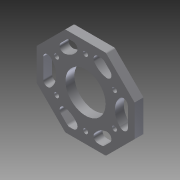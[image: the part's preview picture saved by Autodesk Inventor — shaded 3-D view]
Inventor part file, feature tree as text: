
AUTODESK INVENTOR PART (.ipt)
format: ipt  version: 2012 (Build 160160000, 160)  size: 216,576 bytes
history: native  units: in
note: dims shown in document units (in); Inventor stores cm internally (conversion verified against a paired STEP export)
features: fillet x2, sketch x1, extrude x1
ambient origin geometry x8: Origin, YZ Plane, XZ Plane, XY Plane, X Axis, Y Axis, Z Axis, Center Point
bodies: Solid1 (feature_tree)
feature tree (4):
  sketch  "Sketch1"  dims[d0=2.75in d1=2.5in d2=1.375in d3=1.25in d6=45.0deg d7=45.0deg d8=45.0deg d10=0.136in d11=0.938in d18=1.125in d20=2.3622in d22=360.0deg d24=0.1875in d25=0.1875in d26=0.1875in d27=0.1875in d28=0.1875in d29=0.1875in d30=0.1875in d32=0.1875in d33=0.5in d34=0.25in d35=0.0in d38=0.125in d39=0.125in d40=0.0625in]
  extrude  "Extrusion1"  Depth=2.5in
  fillet  "Fillet1"  Radius=1.375in
  fillet  "Fillet2"  Radius=1.25in
